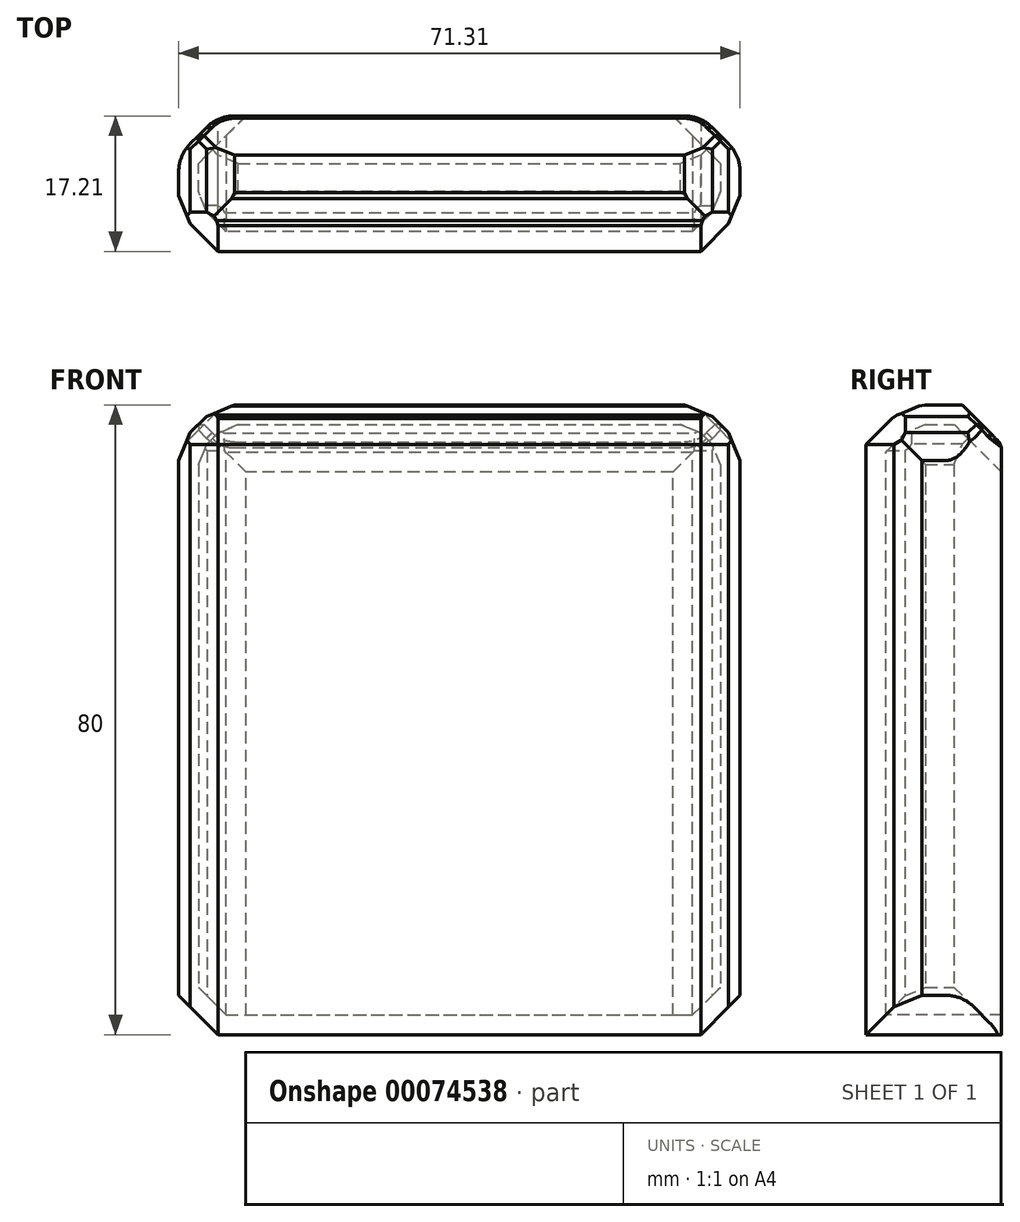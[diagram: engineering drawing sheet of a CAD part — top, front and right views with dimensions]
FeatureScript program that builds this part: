
annotation { "Feature Type Name" : "Feature", "Feature Type Description" : "" }
export const myFeature = defineFeature(function(context is Context, id is Id, definition is map)
    precondition{}
    {
        {
            var Q0;
            Q0=qCreatedBy(makeId("Top.planeOp"),FACE);
            var sketch = newSketch(context, id + "F0", { "sketchPlane" : qUnion([Q0])});
            skLineSegment(sketch, "E0.bottom", {"start": v(-32.27, 0) * mm, "end": v(39.04, 0) * mm});
            skLineSegment(sketch, "E0.top", {"start": v(-32.27, -17.2) * mm, "end": v(39.04, -17.2) * mm});
            skLineSegment(sketch, "E0.left", {"start": v(-32.27, 0) * mm, "end": v(-32.27, -17.2) * mm});
            skLineSegment(sketch, "E0.right", {"start": v(39.04, 0) * mm, "end": v(39.04, -17.2) * mm});
            skSolve(sketch);
        }
        {
            var Q0;
            Q0 = qSketchRegion(id + "F0", true);
            extrude(context, id + "F1", {"entities" : qUnion([Q0]), "depth" : 80 * mm});
        }
        {
            var Q0;
            Q0=makeQuery(id+"F1.opExtrude","CAP_EDGE",EDGE,{"disambiguationData":[OSD([sQuery(id+"F0.wireOp",EDGE,"E0.top")])],"isStart":false});
            var Q1;
            Q1=makeQuery(id+"F1.opExtrude","SWEPT_EDGE",EDGE,{"disambiguationData":[OSD([sQuery(id+"F0.wireOp",EDGE,"E0.top"),sQuery(id+"F0.wireOp",EDGE,"E0.left")])]});
            var Q2;
            Q2=makeQuery(id+"F1.opExtrude","SWEPT_EDGE",EDGE,{"disambiguationData":[OSD([sQuery(id+"F0.wireOp",EDGE,"E0.top"),sQuery(id+"F0.wireOp",EDGE,"E0.right")])]});
            var Q3;
            Q3=makeQuery(id+"F1.opExtrude","CAP_EDGE",EDGE,{"disambiguationData":[OSD([sQuery(id+"F0.wireOp",EDGE,"E0.left")])],"isStart":false});
            var Q4;
            Q4=makeQuery(id+"F1.opExtrude","CAP_EDGE",EDGE,{"disambiguationData":[OSD([sQuery(id+"F0.wireOp",EDGE,"E0.right")])],"isStart":false});
            chamfer(context, id + "F2", {"entities" : qUnion([Q0, Q1, Q2, Q3, Q4]), "width" : 5 * mm, "tangentPropagation" : true});
        }
        {
            var Q0;
            Q0=makeQuery(id+"F1.opExtrude","SWEPT_FACE",FACE,{"disambiguationData":[OSD([sQuery(id+"F0.wireOp",EDGE,"E0.right")])]});
            var Q1;
            Q1=makeQuery(id+"F1.opExtrude","SWEPT_FACE",FACE,{"disambiguationData":[OSD([sQuery(id+"F0.wireOp",EDGE,"E0.left")])]});
            var Q2;
            Q2=makeQuery(id+"F1.opExtrude","CAP_FACE",FACE,{"disambiguationData":[OSD([sQuery(id+"F0.wireOp",EDGE,"E0.bottom"),sQuery(id+"F0.wireOp",EDGE,"E0.top"),sQuery(id+"F0.wireOp",EDGE,"E0.left"),sQuery(id+"F0.wireOp",EDGE,"E0.right")])],"isStart":false});
            chamfer(context, id + "F3", {"entities" : qUnion([Q0, Q1, Q2]), "width" : 5 * mm, "tangentPropagation" : true});
        }
        {
            var Q0;
            Q0=makeQuery(id+"F1.opExtrude","SWEPT_FACE",FACE,{"disambiguationData":[OSD([sQuery(id+"F0.wireOp",EDGE,"E0.bottom")])]});
            shell(context, id + "F4", {"entities" : qUnion([Q0]), "thickness" : 2.5 * mm});
        }
        {
            var Q0;
            {var subQ0=sQuery(id+"F0.wireOp",EDGE,"E0.bottom");Q0=makeQuery(id+"F3.opChamfer","BLEND_EDGE",EDGE,{"blendedFrom":[makeQuery(id+"F1.opExtrude","SWEPT_EDGE",EDGE,{"disambiguationData":[OSD([subQ0,sQuery(id+"F0.wireOp",EDGE,"E0.right")])]}),makeQuery(id+"F1.opExtrude","SWEPT_FACE",FACE,{"disambiguationData":[OSD([subQ0])]})],"blendedInto":[makeQuery(id+"F1.opExtrude","SWEPT_FACE",FACE,{"disambiguationData":[OSD([subQ0])]})]});}
            var Q1;
            {var subQ0=sQuery(id+"F0.wireOp",EDGE,"E0.bottom");Q1=makeQuery(id+"F3.opChamfer","BLEND_EDGE",EDGE,{"blendedFrom":[makeQuery(id+"F1.opExtrude","SWEPT_EDGE",EDGE,{"disambiguationData":[OSD([subQ0,sQuery(id+"F0.wireOp",EDGE,"E0.left")])]}),makeQuery(id+"F1.opExtrude","SWEPT_FACE",FACE,{"disambiguationData":[OSD([subQ0])]})],"blendedInto":[makeQuery(id+"F1.opExtrude","SWEPT_FACE",FACE,{"disambiguationData":[OSD([subQ0])]})]});}
            fillet(context, id + "F5", {"entities" : qUnion([Q0, Q1]), "radius" : 5 * mm, "tangentPropagation" : true, "allowEdgeOverflow" : false});
        }
        {
            var Q0;
            {var subQ0=sQuery(id+"F0.wireOp",EDGE,"E0.top");var subQ1=makeQuery(id+"F1.opExtrude","CAP_FACE",FACE,{"disambiguationData":[OSD([sQuery(id+"F0.wireOp",EDGE,"E0.bottom"),subQ0,sQuery(id+"F0.wireOp",EDGE,"E0.left"),sQuery(id+"F0.wireOp",EDGE,"E0.right")])],"isStart":false});Q0=makeQuery(id+"F3.opChamfer","BLEND_EDGE",EDGE,{"blendedFrom":[makeQuery(id+"F2.opChamfer","BLEND_EDGE",EDGE,{"blendedFrom":[makeQuery(id+"F1.opExtrude","CAP_EDGE",EDGE,{"disambiguationData":[OSD([subQ0])],"isStart":false}),subQ1],"blendedInto":[subQ1]}),subQ1],"blendedInto":[subQ1]});}
            var Q1;
            {var subQ0=sQuery(id+"F0.wireOp",EDGE,"E0.top");Q1=makeQuery(id+"F3.opChamfer","BLEND_EDGE",EDGE,{"blendedFrom":[makeQuery(id+"F2.opChamfer","BLEND_EDGE",EDGE,{"blendedFrom":[makeQuery(id+"F1.opExtrude","CAP_EDGE",EDGE,{"disambiguationData":[OSD([subQ0])],"isStart":false}),makeQuery(id+"F1.opExtrude","CAP_FACE",FACE,{"disambiguationData":[OSD([sQuery(id+"F0.wireOp",EDGE,"E0.bottom"),subQ0,sQuery(id+"F0.wireOp",EDGE,"E0.left"),sQuery(id+"F0.wireOp",EDGE,"E0.right")])],"isStart":false})],"blendedInto":[makeQuery(id+"F1.opExtrude","CAP_FACE",FACE,{"disambiguationData":[OSD([sQuery(id+"F0.wireOp",EDGE,"E0.bottom"),subQ0,sQuery(id+"F0.wireOp",EDGE,"E0.left"),sQuery(id+"F0.wireOp",EDGE,"E0.right")])],"isStart":false})]}),makeQuery(id+"F2.opChamfer","BLEND_FACE",FACE,{"disambiguationData":[OSD([subQ0])]})],"blendedInto":[makeQuery(id+"F2.opChamfer","BLEND_FACE",FACE,{"disambiguationData":[OSD([subQ0])]})]});}
            chamfer(context, id + "F6", {"entities" : qUnion([Q0, Q1]), "width" : 2 * mm, "tangentPropagation" : true});
        }
        {
            var Q0;
            {var subQ0=sQuery(id+"F0.wireOp",EDGE,"E0.left");Q0=makeQuery(id+"F3.opChamfer","BLEND_EDGE",EDGE,{"blendedFrom":[makeQuery(id+"F1.opExtrude","SWEPT_EDGE",EDGE,{"disambiguationData":[OSD([sQuery(id+"F0.wireOp",EDGE,"E0.bottom"),subQ0])]}),makeQuery(id+"F2.opChamfer","BLEND_FACE",FACE,{"disambiguationData":[OSD([subQ0])]})],"blendedInto":[makeQuery(id+"F2.opChamfer","BLEND_FACE",FACE,{"disambiguationData":[OSD([subQ0])]})]});}
            var Q1;
            Q1=makeQuery(id+"F3.opChamfer","BLEND_EDGE",EDGE,{"blendedFrom":[makeQuery(id+"F1.opExtrude","CAP_EDGE",EDGE,{"disambiguationData":[OSD([sQuery(id+"F0.wireOp",EDGE,"E0.bottom")])],"isStart":false}),makeQuery(id+"F2.opChamfer","BLEND_FACE",FACE,{"disambiguationData":[OSD([sQuery(id+"F0.wireOp",EDGE,"E0.left")])]})],"blendedInto":[makeQuery(id+"F2.opChamfer","BLEND_FACE",FACE,{"disambiguationData":[OSD([sQuery(id+"F0.wireOp",EDGE,"E0.left")])]})]});
            var Q2;
            {var subQ0=sQuery(id+"F0.wireOp",EDGE,"E0.bottom");Q2=makeQuery(id+"F3.opChamfer","BLEND_EDGE",EDGE,{"blendedFrom":[makeQuery(id+"F1.opExtrude","SWEPT_EDGE",EDGE,{"disambiguationData":[OSD([subQ0,sQuery(id+"F0.wireOp",EDGE,"E0.left")])]}),makeQuery(id+"F1.opExtrude","CAP_EDGE",EDGE,{"disambiguationData":[OSD([subQ0])],"isStart":false})],"blendedInto":[]});}
            var Q3;
            {var subQ0=sQuery(id+"F0.wireOp",EDGE,"E0.bottom");Q3=makeQuery(id+"F3.opChamfer","BLEND_EDGE",EDGE,{"blendedFrom":[makeQuery(id+"F1.opExtrude","SWEPT_EDGE",EDGE,{"disambiguationData":[OSD([subQ0,sQuery(id+"F0.wireOp",EDGE,"E0.right")])]}),makeQuery(id+"F1.opExtrude","CAP_EDGE",EDGE,{"disambiguationData":[OSD([subQ0])],"isStart":false})],"blendedInto":[]});}
            var Q4;
            Q4=makeQuery(id+"F3.opChamfer","BLEND_EDGE",EDGE,{"blendedFrom":[makeQuery(id+"F1.opExtrude","CAP_EDGE",EDGE,{"disambiguationData":[OSD([sQuery(id+"F0.wireOp",EDGE,"E0.bottom")])],"isStart":false}),makeQuery(id+"F2.opChamfer","BLEND_FACE",FACE,{"disambiguationData":[OSD([sQuery(id+"F0.wireOp",EDGE,"E0.right")])]})],"blendedInto":[makeQuery(id+"F2.opChamfer","BLEND_FACE",FACE,{"disambiguationData":[OSD([sQuery(id+"F0.wireOp",EDGE,"E0.right")])]})]});
            var Q5;
            {var subQ0=sQuery(id+"F0.wireOp",EDGE,"E0.right");Q5=makeQuery(id+"F3.opChamfer","BLEND_EDGE",EDGE,{"blendedFrom":[makeQuery(id+"F1.opExtrude","SWEPT_EDGE",EDGE,{"disambiguationData":[OSD([sQuery(id+"F0.wireOp",EDGE,"E0.bottom"),subQ0])]}),makeQuery(id+"F2.opChamfer","BLEND_FACE",FACE,{"disambiguationData":[OSD([subQ0])]})],"blendedInto":[makeQuery(id+"F2.opChamfer","BLEND_FACE",FACE,{"disambiguationData":[OSD([subQ0])]})]});}
            chamfer(context, id + "F7", {"entities" : qUnion([Q0, Q1, Q2, Q3, Q4, Q5]), "width" : 1 * mm, "tangentPropagation" : true});
        }
        {
            var Q0;
            {var subQ0=sQuery(id+"F0.wireOp",EDGE,"E0.right");Q0=makeQuery(id+"F3.opChamfer","BLEND_EDGE",EDGE,{"blendedFrom":[makeQuery(id+"F1.opExtrude","SWEPT_EDGE",EDGE,{"disambiguationData":[OSD([sQuery(id+"F0.wireOp",EDGE,"E0.bottom"),subQ0])]}),makeQuery(id+"F1.opExtrude","SWEPT_FACE",FACE,{"disambiguationData":[OSD([subQ0])]})],"blendedInto":[makeQuery(id+"F1.opExtrude","SWEPT_FACE",FACE,{"disambiguationData":[OSD([subQ0])]})]});}
            var Q1;
            {var subQ0=sQuery(id+"F0.wireOp",EDGE,"E0.left");Q1=makeQuery(id+"F3.opChamfer","BLEND_EDGE",EDGE,{"blendedFrom":[makeQuery(id+"F1.opExtrude","SWEPT_EDGE",EDGE,{"disambiguationData":[OSD([sQuery(id+"F0.wireOp",EDGE,"E0.bottom"),subQ0])]}),makeQuery(id+"F1.opExtrude","SWEPT_FACE",FACE,{"disambiguationData":[OSD([subQ0])]})],"blendedInto":[makeQuery(id+"F1.opExtrude","SWEPT_FACE",FACE,{"disambiguationData":[OSD([subQ0])]})]});}
            fillet(context, id + "F8", {"entities" : qUnion([Q0, Q1]), "radius" : 5 * mm, "tangentPropagation" : true, "allowEdgeOverflow" : false});
        }
    });
